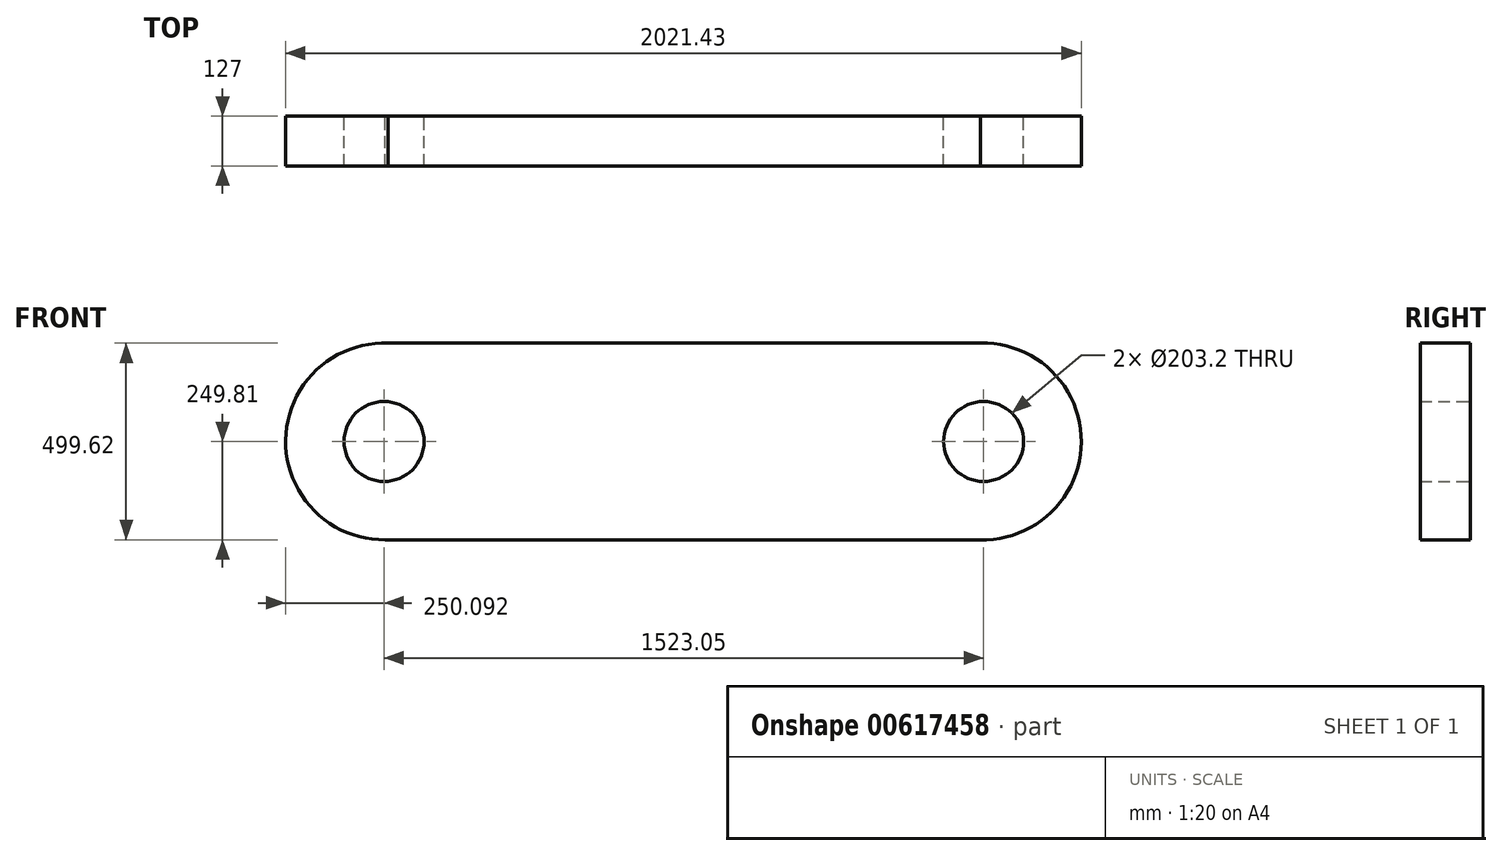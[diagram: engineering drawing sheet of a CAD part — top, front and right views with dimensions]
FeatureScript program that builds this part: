
annotation { "Feature Type Name" : "Feature", "Feature Type Description" : "" }
export const myFeature = defineFeature(function(context is Context, id is Id, definition is map)
    precondition{}
    {
        {
            var Q0;
            Q0=qCreatedBy(makeId("Front.planeOp"),FACE);
            var sketch = newSketch(context, id + "F0", { "sketchPlane" : qUnion([Q0])});
            skLineSegment(sketch, "E0", {"start": v(-727.28, 0) * mm, "end": v(796.72, 0) * mm});
            skCircle(sketch, "E1", {"center": v(-725.82, 0) * mm, "radius": 249.8 * mm});
            skCircle(sketch, "E2", {"center": v(795.99, 0) * mm, "radius": 249.8 * mm});
            skCircle(sketch, "E3", {"center": v(797.52, 0) * mm, "radius": 101.6 * mm});
            skCircle(sketch, "E4", {"center": v(-725.54, 0) * mm, "radius": 101.6 * mm});
            skLineSegment(sketch, "E5", {"start": v(803.63, -249.7) * mm, "end": v(-728.67, -249.8) * mm});
            skLineSegment(sketch, "E6", {"start": v(789.96, 249.74) * mm, "end": v(-715, 249.57) * mm});
            skSolve(sketch);
        }
        {
            var Q0;
            Q0 = qSketchRegion(id + "F0", true);
            extrude(context, id + "F1", {"entities" : qUnion([Q0]), "depth" : 127 * mm, "offsetDistance" : 25.4 * mm});
        }
    });
